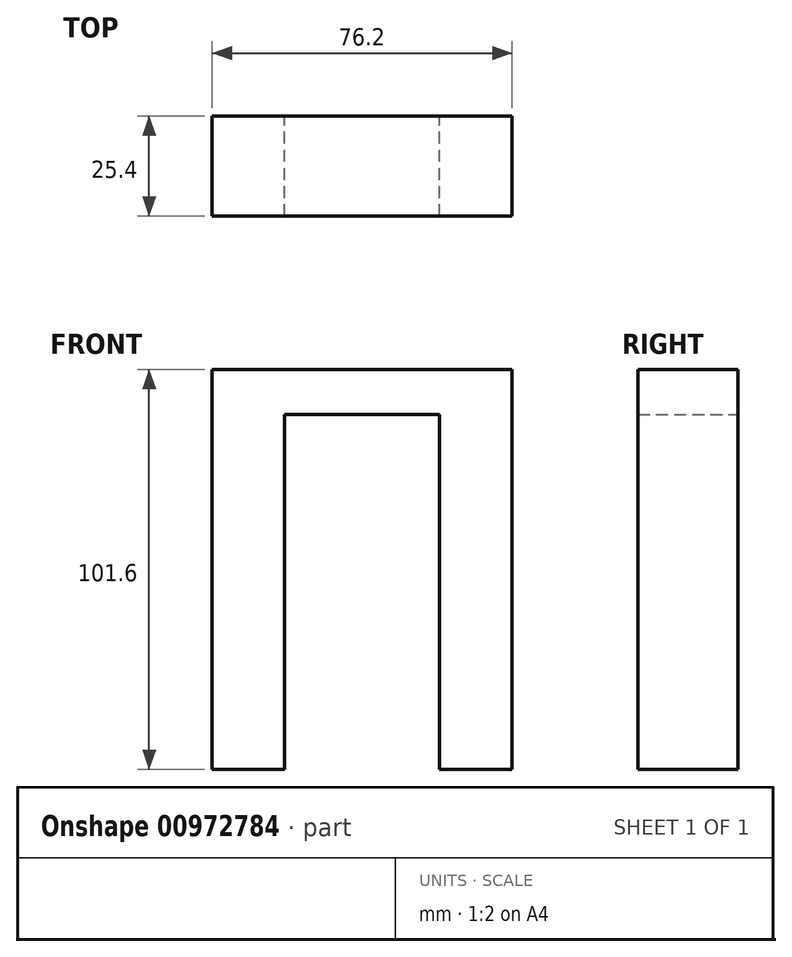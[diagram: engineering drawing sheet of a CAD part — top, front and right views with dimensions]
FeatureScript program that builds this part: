
annotation { "Feature Type Name" : "Feature", "Feature Type Description" : "" }
export const myFeature = defineFeature(function(context is Context, id is Id, definition is map)
    precondition{}
    {
        {
            var Q0;
            Q0=qCreatedBy(makeId("Front.planeOp"),FACE);
            var sketch = newSketch(context, id + "F0", { "sketchPlane" : qUnion([Q0])});
            skLineSegment(sketch, "E0.bottom", {"start": v(-38.1, 0) * mm, "end": v(38.1, 0) * mm});
            skLineSegment(sketch, "E0.top", {"start": v(-38.1, 101.6) * mm, "end": v(38.1, 101.6) * mm});
            skLineSegment(sketch, "E0.left", {"start": v(-38.1, 0) * mm, "end": v(-38.1, 101.6) * mm});
            skLineSegment(sketch, "E0.right", {"start": v(38.1, 0) * mm, "end": v(38.1, 101.6) * mm});
            skLineSegment(sketch, "E1", {"start": v(0, 101.6) * mm, "end": v(0, 0) * mm, "construction": true});
            skLineSegment(sketch, "E2.bottom", {"start": v(19.68, 90.17) * mm, "end": v(-19.69, 90.17) * mm});
            skLineSegment(sketch, "E2.left", {"start": v(19.69, 90.17) * mm, "end": v(19.69, 0) * mm});
            skLineSegment(sketch, "E2.right", {"start": v(-19.69, 90.17) * mm, "end": v(-19.68, 0) * mm});
            skPoint(sketch, "E2.middle", {"position": v(0, 0) * mm});
            skLineSegment(sketch, "E3", {"start": v(0, 0) * mm, "end": v(-19.68, 0) * mm, "construction": true});
            skSolve(sketch);
        }
        {
            var Q0;
            Q0=makeQuery(id+"F0.imprint","IMPRINT",FACE,{"disambiguationData":[TD([[makeQuery(id+"F0.imprint","IMPRINT",EDGE,{"derivedFrom":sQuery(id+"F0.wireOp",EDGE,"E0.top")}),-1.0]])]});
            extrude(context, id + "F1", {"entities" : qUnion([Q0]), "depth" : 25.4 * mm, "offsetDistance" : 25.4 * mm});
        }
    });
